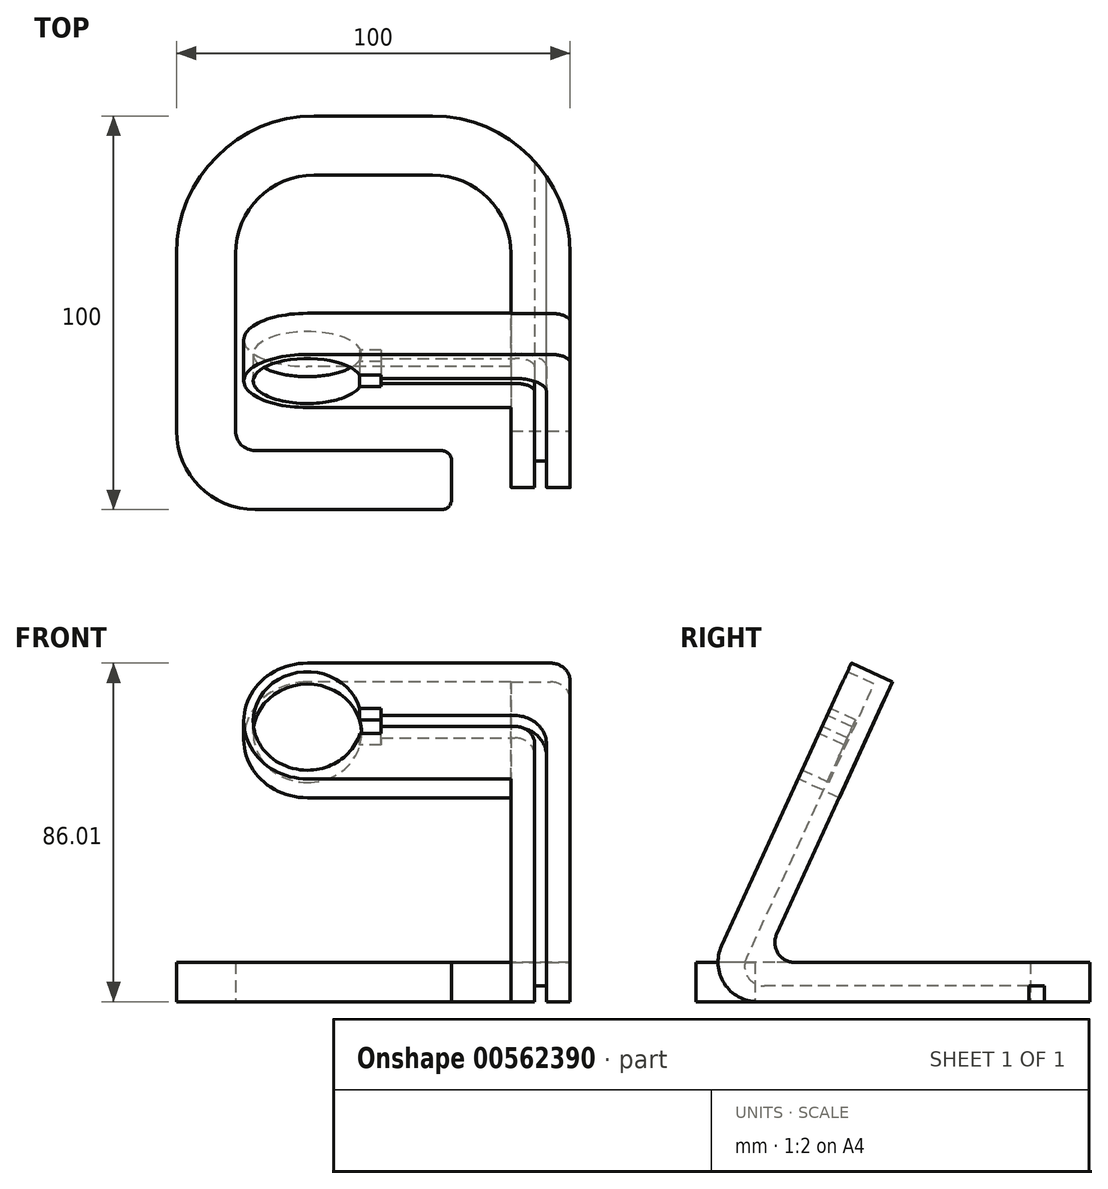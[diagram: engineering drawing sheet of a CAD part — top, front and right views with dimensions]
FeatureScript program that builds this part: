
annotation { "Feature Type Name" : "Feature", "Feature Type Description" : "" }
export const myFeature = defineFeature(function(context is Context, id is Id, definition is map)
    precondition{}
    {
        {
            var Q0;
            Q0=qCreatedBy(makeId("Top.planeOp"),FACE);
            var sketch = newSketch(context, id + "F0", { "sketchPlane" : qUnion([Q0])});
            skLineSegment(sketch, "E0.bottom", {"start": v(15, 50) * mm, "end": v(-15, 50) * mm});
            skLineSegment(sketch, "E0.top", {"start": v(50, -50) * mm, "end": v(35, -50) * mm});
            skLineSegment(sketch, "E0.left", {"start": v(50, 15) * mm, "end": v(50, -50) * mm});
            skLineSegment(sketch, "E0.right", {"start": v(-50, 15) * mm, "end": v(-50, -30) * mm});
            skPoint(sketch, "E0.middle", {"position": v(0, 0) * mm});
            skPoint(sketch, "E1.visualSharp", {"position": v(-50, -50) * mm});
            skArc(sketch, "E1.filletArc", {"start": v(-50, -30) * mm, "mid": v(-44.14, -44.14) * mm, "end": v(-30, -50) * mm});
            skPoint(sketch, "E2.visualSharp", {"position": v(-50, 50) * mm});
            skArc(sketch, "E2.filletArc", {"start": v(-15, 50) * mm, "mid": v(-39.75, 39.75) * mm, "end": v(-50, 15) * mm});
            skPoint(sketch, "E3.visualSharp", {"position": v(50, -50) * mm});
            skPoint(sketch, "E4.visualSharp", {"position": v(50, 50) * mm});
            skArc(sketch, "E4.filletArc", {"start": v(50, 15) * mm, "mid": v(39.75, 39.75) * mm, "end": v(15, 50) * mm});
            skLineSegment(sketch, "E5.0", {"start": v(-35, 15) * mm, "end": v(-35, -30) * mm});
            skLineSegment(sketch, "E6.0", {"start": v(17.36, -35) * mm, "end": v(-30, -35) * mm});
            skLineSegment(sketch, "E7.0", {"start": v(35, 15) * mm, "end": v(35, -35) * mm});
            skLineSegment(sketch, "E8.0", {"start": v(15, 35) * mm, "end": v(-15, 35) * mm});
            skPoint(sketch, "E9.visualSharp", {"position": v(-35, -35) * mm});
            skArc(sketch, "E9.filletArc", {"start": v(-35, -30) * mm, "mid": v(-33.54, -33.54) * mm, "end": v(-30, -35) * mm});
            skPoint(sketch, "E10.visualSharp", {"position": v(-35, 35) * mm});
            skArc(sketch, "E10.filletArc", {"start": v(-15, 35) * mm, "mid": v(-29.14, 29.14) * mm, "end": v(-35, 15) * mm});
            skPoint(sketch, "E11.visualSharp", {"position": v(35, 35) * mm});
            skArc(sketch, "E11.filletArc", {"start": v(35, 15) * mm, "mid": v(29.14, 29.14) * mm, "end": v(15, 35) * mm});
            skLineSegment(sketch, "E12", {"start": v(19.86, -37.5) * mm, "end": v(19.86, -47.5) * mm});
            skLineSegment(sketch, "E13", {"start": v(35, -50) * mm, "end": v(35, -35) * mm});
            skLineSegment(sketch, "E14.trimOffspring", {"start": v(17.36, -50) * mm, "end": v(-30, -50) * mm});
            skPoint(sketch, "E15.visualSharp", {"position": v(19.86, -35) * mm});
            skArc(sketch, "E15.filletArc", {"start": v(19.86, -37.5) * mm, "mid": v(19.13, -35.73) * mm, "end": v(17.36, -35) * mm});
            skPoint(sketch, "E16.visualSharp", {"position": v(19.86, -50) * mm});
            skArc(sketch, "E16.filletArc", {"start": v(17.36, -50) * mm, "mid": v(19.13, -49.27) * mm, "end": v(19.86, -47.5) * mm});
            skSolve(sketch);
        }
        {
            var Q0;
            Q0=makeQuery(id+"F0.imprint","IMPRINT",FACE,{"disambiguationData":[TD([[makeQuery(id+"F0.imprint","IMPRINT",EDGE,{"derivedFrom":sQuery(id+"F0.wireOp",EDGE,"E0.bottom")}),1.0]])]});
            extrude(context, id + "F1", {"entities" : qUnion([Q0]), "depth" : 10 * mm, "offsetDistance" : 25 * mm});
        }
        {
            var Q0;
            Q0=makeQuery(id+"F1.opExtrude","SWEPT_FACE",FACE,{"disambiguationData":[OSD([sQuery(id+"F0.wireOp",EDGE,"E0.left")])]});
            var sketch = newSketch(context, id + "F2", { "sketchPlane" : qUnion([Q0])});
            skLineSegment(sketch, "E17", {"start": v(-43.5, 14.17) * mm, "end": v(-10.57, 86.01) * mm});
            skLineSegment(sketch, "E18", {"start": v(-10.57, 86.01) * mm, "end": v(-0.13, 81.23) * mm});
            skLineSegment(sketch, "E19", {"start": v(-0.13, 81.23) * mm, "end": v(-29.53, 17.08) * mm});
            skLineSegment(sketch, "E20", {"start": v(-18.45, 10) * mm, "end": v(-24.99, 10) * mm});
            skLineSegment(sketch, "E21", {"start": v(-18.45, 0) * mm, "end": v(-34.41, 0) * mm});
            skLineSegment(sketch, "E22", {"start": v(-18.45, 0) * mm, "end": v(-18.45, 10) * mm});
            skArc(sketch, "E23.filletArc", {"start": v(-29.53, 17.08) * mm, "mid": v(-29.2, 12.3) * mm, "end": v(-24.99, 10) * mm});
            skPoint(sketch, "E24.visualSharp", {"position": v(-50, 0) * mm});
            skArc(sketch, "E24.filletArc", {"start": v(-43.5, 14.17) * mm, "mid": v(-42.83, 4.6) * mm, "end": v(-34.41, 0) * mm});
            skSolve(sketch);
        }
        {
            var Q0;
            {var subQ1=sQuery(id+"F0.wireOp",EDGE,"E0.left");var subQ6=makeQuery(id+"F1.opExtrude","SWEPT_EDGE",EDGE,{"disambiguationData":[OSD([sQuery(id+"F0.wireOp",EDGE,"E0.top"),subQ1])]});Q0=makeQuery(id+"F2.imprint","IMPRINT",FACE,{"disambiguationData":[TD([[makeQuery(id+"F2.imprint","IMPRINT",EDGE,{"derivedFrom":subQ6}),1.0]])]});}
            extrude(context, id + "F3", {"entities" : qUnion([Q0]), "operationType" : NewBodyOperationType.REMOVE, "oppositeDirection" : true, "depth" : 25 * mm, "offsetDistance" : 25 * mm});
        }
        {
            var Q0;
            {var subQ1=sQuery(id+"F2.wireOp",EDGE,"E17");Q0=makeQuery(id+"F2.imprint","IMPRINT",FACE,{"disambiguationData":[TD([[makeQuery(id+"F2.imprint","IMPRINT",EDGE,{"derivedFrom":subQ1}),-1.0]])]});}
            extrude(context, id + "F4", {"entities" : qUnion([Q0]), "operationType" : NewBodyOperationType.ADD, "oppositeDirection" : true, "depth" : 15 * mm, "offsetDistance" : 25 * mm});
        }
        {
            var Q0;
            Q0=makeQuery(id+"F4.opExtrude","SWEPT_FACE",FACE,{"disambiguationData":[OSD([sQuery(id+"F2.wireOp",EDGE,"E17")])]});
            var sketch = newSketch(context, id + "F5", { "sketchPlane" : qUnion([Q0])});
            skLineSegment(sketch, "E25.bottom", {"start": v(50, 73.79) * mm, "end": v(-16.75, 73.79) * mm});
            skLineSegment(sketch, "E25.top", {"start": v(50, 41.44) * mm, "end": v(-16.75, 41.44) * mm});
            skLineSegment(sketch, "E25.left", {"start": v(50, 73.79) * mm, "end": v(50, 41.44) * mm});
            skCircle(sketch, "E26", {"center": v(-16.75, 57.61) * mm, "radius": 16.17 * mm});
            skPoint(sketch, "E27.visualSharp", {"position": v(50, 73.79) * mm});
            skCircle(sketch, "E28", {"center": v(-16.75, 57.61) * mm, "radius": 13.75 * mm});
            skSolve(sketch);
        }
        {
            var Q0;
            Q0=makeQuery(id+"F5.imprint","IMPRINT",FACE,{"disambiguationData":[TD([[makeQuery(id+"F5.imprint","IMPRINT",EDGE,{"derivedFrom":sQuery(id+"F5.wireOp",EDGE,"E28")}),-1.0]])]});
            var Q1;
            Q1=makeQuery(id+"F5.imprint","IMPRINT",FACE,{"disambiguationData":[TD([[makeQuery(id+"F5.imprint","IMPRINT",EDGE,{"derivedFrom":sQuery(id+"F5.wireOp",EDGE,"E28")}),1.0]])]});
            var Q2;
            Q2=makeQuery(id+"F5.imprint","IMPRINT",FACE,{"disambiguationData":[TD([[makeQuery(id+"F5.imprint","IMPRINT",EDGE,{"derivedFrom":sQuery(id+"F5.wireOp",EDGE,"ab50c3b4-7159-4a78-a1d6-39594553cd38")}),1.0]])]});
            var Q3;
            {var subQ0=sQuery(id+"F5.wireOp",EDGE,"E25.bottom");var subQ3=sQuery(id+"F5.wireOp",EDGE,"E26");var subQ4=makeQuery(id+"F5.imprint","INTERSECT",VERTEX,{"derivedFrom":[subQ0,subQ3]});Q3=makeQuery(id+"F5.imprint","IMPRINT",FACE,{"disambiguationData":[TD([[makeQuery(id+"F5.imprint","IMPRINT",EDGE,{"disambiguationData":[TD([[subQ4,1.0]])],"derivedFrom":subQ0}),1.0]])]});}
            extrude(context, id + "F6", {"entities" : qUnion([Q0, Q1, Q2, Q3]), "operationType" : NewBodyOperationType.ADD, "oppositeDirection" : true, "depth" : 11.5 * mm, "offsetDistance" : 25 * mm});
        }
        {
            var Q0;
            Q0=makeQuery(id+"F5.imprint","IMPRINT",FACE,{"disambiguationData":[TD([[makeQuery(id+"F5.imprint","IMPRINT",EDGE,{"derivedFrom":sQuery(id+"F5.wireOp",EDGE,"ab50c3b4-7159-4a78-a1d6-39594553cd38")}),1.0]])]});
            var Q1;
            Q1=makeQuery(id+"F5.imprint","IMPRINT",FACE,{"disambiguationData":[TD([[makeQuery(id+"F5.imprint","IMPRINT",EDGE,{"derivedFrom":sQuery(id+"F5.wireOp",EDGE,"E28")}),1.0]])]});
            extrude(context, id + "F7", {"entities" : qUnion([Q0, Q1]), "operationType" : NewBodyOperationType.REMOVE, "oppositeDirection" : true, "depth" : 7.5 * mm, "offsetDistance" : 25 * mm});
        }
        {
            var Q0;
            {var subQ0=sQuery(id+"F2.wireOp",EDGE,"E17");Q0=makeQuery(id+"F6.boolean.opBoolean","MERGE",FACE,{"derivedFrom":[makeQuery(id+"F4.opExtrude","SWEPT_FACE",FACE,{"disambiguationData":[OSD([subQ0])]}),makeQuery(id+"F6.opExtrude","CAP_FACE",FACE,{"disambiguationData":[OSD([subQ0,sQuery(id+"F5.wireOp",EDGE,"E25.bottom"),sQuery(id+"F5.wireOp",EDGE,"E25.top"),sQuery(id+"F5.wireOp",EDGE,"E26")])],"isStart":true})]});}
            var sketch = newSketch(context, id + "F8", { "sketchPlane" : qUnion([Q0])});
            skLineSegment(sketch, "E29", {"start": v(-3, 57.61) * mm, "end": v(42.5, 57.61) * mm, "construction": true});
            skPoint(sketch, "E29.startSnap0", {"position": v(-32.92, 57.61) * mm});
            skLineSegment(sketch, "E30", {"start": v(42.5, 57.61) * mm, "end": v(42.5, -17.42) * mm, "construction": true});
            skPoint(sketch, "E30.startSnap0", {"position": v(42.5, -5.25) * mm});
            skPoint(sketch, "E30.endSnap0", {"position": v(42.5, -5.25) * mm});
            skLineSegment(sketch, "E31", {"start": v(2, 59.11) * mm, "end": v(36, 59.11) * mm});
            skLineSegment(sketch, "E32", {"start": v(2, 56.11) * mm, "end": v(36, 56.11) * mm});
            skLineSegment(sketch, "E33", {"start": v(2, 59.11) * mm, "end": v(2, 56.11) * mm});
            skLineSegment(sketch, "E34.bottom", {"start": v(2, 61.11) * mm, "end": v(-6.68, 61.11) * mm});
            skLineSegment(sketch, "E34.top", {"start": v(2, 54.11) * mm, "end": v(-6.68, 54.11) * mm});
            skLineSegment(sketch, "E34.left", {"start": v(2, 61.11) * mm, "end": v(2, 54.11) * mm});
            skLineSegment(sketch, "E34.right", {"start": v(-6.68, 61.11) * mm, "end": v(-6.68, 54.11) * mm});
            skLineSegment(sketch, "E35", {"start": v(41, 51.11) * mm, "end": v(41, -17.42) * mm});
            skLineSegment(sketch, "E36", {"start": v(41, -17.42) * mm, "end": v(44, -17.42) * mm});
            skLineSegment(sketch, "E37", {"start": v(44, -17.42) * mm, "end": v(44, 51.11) * mm});
            skPoint(sketch, "E38.visualSharp", {"position": v(41, 56.11) * mm});
            skArc(sketch, "E38.filletArc", {"start": v(41, 51.11) * mm, "mid": v(39.54, 54.65) * mm, "end": v(36, 56.11) * mm});
            skPoint(sketch, "E39.visualSharp", {"position": v(44, 59.11) * mm});
            skArc(sketch, "E39.filletArc", {"start": v(44, 51.11) * mm, "mid": v(41.66, 56.77) * mm, "end": v(36, 59.11) * mm});
            skSolve(sketch);
        }
        {
            var Q0;
            {var subQ0=sQuery(id+"F8.wireOp",EDGE,"E34.left");var subQ2=sQuery(id+"F8.wireOp",EDGE,"E34.bottom");var subQ3=makeQuery(id+"F8.imprint","INTERSECT",VERTEX,{"derivedFrom":[subQ2,subQ0]});Q0=makeQuery(id+"F8.imprint","IMPRINT",FACE,{"disambiguationData":[TD([[makeQuery(id+"F8.imprint","IMPRINT",EDGE,{"disambiguationData":[TD([[subQ3,-1.0]])],"derivedFrom":subQ2}),1.0]])]});}
            var Q1;
            {var subQ1=sQuery(id+"F8.wireOp",EDGE,"E31");Q1=makeQuery(id+"F8.imprint","IMPRINT",FACE,{"disambiguationData":[TD([[makeQuery(id+"F8.imprint","IMPRINT",EDGE,{"derivedFrom":subQ1}),-1.0]])]});}
            var Q2;
            {var subQ0=sQuery(id+"F8.wireOp",EDGE,"E36");Q2=makeQuery(id+"F8.imprint","IMPRINT",FACE,{"disambiguationData":[TD([[makeQuery(id+"F8.imprint","IMPRINT",EDGE,{"derivedFrom":subQ0}),1.0]])]});}
            extrude(context, id + "F9", {"entities" : qUnion([Q0, Q1, Q2]), "operationType" : NewBodyOperationType.REMOVE, "oppositeDirection" : true, "depth" : 7 * mm, "offsetDistance" : 25 * mm});
        }
        {
            var Q0;
            Q0=makeQuery(id+"F1.opExtrude","CAP_FACE",FACE,{"disambiguationData":[OSD([sQuery(id+"F0.wireOp",EDGE,"E0.bottom"),sQuery(id+"F0.wireOp",EDGE,"E0.top"),sQuery(id+"F0.wireOp",EDGE,"E0.left"),sQuery(id+"F0.wireOp",EDGE,"E0.right"),sQuery(id+"F0.wireOp",EDGE,"E1.filletArc"),sQuery(id+"F0.wireOp",EDGE,"E2.filletArc"),sQuery(id+"F0.wireOp",EDGE,"E4.filletArc"),sQuery(id+"F0.wireOp",EDGE,"E5.0"),sQuery(id+"F0.wireOp",EDGE,"E6.0"),sQuery(id+"F0.wireOp",EDGE,"E7.0"),sQuery(id+"F0.wireOp",EDGE,"E8.0"),sQuery(id+"F0.wireOp",EDGE,"E9.filletArc"),sQuery(id+"F0.wireOp",EDGE,"E10.filletArc"),sQuery(id+"F0.wireOp",EDGE,"E11.filletArc"),sQuery(id+"F0.wireOp",EDGE,"E12"),sQuery(id+"F0.wireOp",EDGE,"E13"),sQuery(id+"F0.wireOp",EDGE,"E14.trimOffspring"),sQuery(id+"F0.wireOp",EDGE,"E15.filletArc"),sQuery(id+"F0.wireOp",EDGE,"E16.filletArc")])],"isStart":true});
            var sketch = newSketch(context, id + "F10", { "sketchPlane" : qUnion([Q0])});
            skLineSegment(sketch, "E40", {"start": v(42.5, 34.41) * mm, "end": v(42.5, -49.23) * mm, "construction": true});
            skLineSegment(sketch, "E41", {"start": v(41, 34.41) * mm, "end": v(41, -49.23) * mm});
            skLineSegment(sketch, "E42", {"start": v(44, -49.23) * mm, "end": v(44, 34.41) * mm});
            skLineSegment(sketch, "E43", {"start": v(41, 34.41) * mm, "end": v(41, 42.4) * mm});
            skLineSegment(sketch, "E44", {"start": v(41, 42.4) * mm, "end": v(44, 42.4) * mm});
            skLineSegment(sketch, "E45", {"start": v(44, 42.4) * mm, "end": v(44, 34.41) * mm});
            skLineSegment(sketch, "E46", {"start": v(41, 34.41) * mm, "end": v(44, 34.41) * mm});
            skSolve(sketch);
        }
        {
            var Q0;
            Q0=makeQuery(id+"F10.imprint","IMPRINT",FACE,{"disambiguationData":[TD([[makeQuery(id+"F10.imprint","IMPRINT",EDGE,{"derivedFrom":sQuery(id+"F10.wireOp",EDGE,"E43")}),-1.0]])]});
            var Q1;
            {var subQ0=sQuery(id+"F10.wireOp",EDGE,"E46");Q1=makeQuery(id+"F10.imprint","IMPRINT",FACE,{"disambiguationData":[TD([[makeQuery(id+"F10.imprint","IMPRINT",EDGE,{"derivedFrom":subQ0}),-1.0]])]});}
            extrude(context, id + "F11", {"entities" : qUnion([Q0, Q1]), "operationType" : NewBodyOperationType.REMOVE, "oppositeDirection" : true, "depth" : 4 * mm, "offsetDistance" : 25 * mm});
        }
        {
            var Q0;
            Q0=makeQuery(id+"F11.boolean.opBoolean","INTERSECT",EDGE,{"derivedFrom":[makeQuery(id+"F9.boolean.opBoolean","COPY",FACE,{"derivedFrom":makeQuery(id+"F9.opExtrude","CAP_FACE",FACE,{"disambiguationData":[OSD([sQuery(id+"F5.wireOp",EDGE,"E28"),sQuery(id+"F8.wireOp",EDGE,"E31"),sQuery(id+"F8.wireOp",EDGE,"E32"),sQuery(id+"F8.wireOp",EDGE,"E34.bottom"),sQuery(id+"F8.wireOp",EDGE,"E34.top"),sQuery(id+"F8.wireOp",EDGE,"E34.left"),sQuery(id+"F8.wireOp",EDGE,"E35"),sQuery(id+"F8.wireOp",EDGE,"E36"),sQuery(id+"F8.wireOp",EDGE,"E37"),sQuery(id+"F8.wireOp",EDGE,"E38.filletArc"),sQuery(id+"F8.wireOp",EDGE,"E39.filletArc")])],"isStart":false})}),makeQuery(id+"F11.opExtrude","CAP_FACE",FACE,{"disambiguationData":[OSD([sQuery(id+"F0.wireOp",EDGE,"E4.filletArc"),sQuery(id+"F10.wireOp",EDGE,"E41"),sQuery(id+"F10.wireOp",EDGE,"E42"),sQuery(id+"F10.wireOp",EDGE,"E43"),sQuery(id+"F10.wireOp",EDGE,"E44"),sQuery(id+"F10.wireOp",EDGE,"E45")])],"isStart":false})]});
            fillet(context, id + "F12", {"entities" : qUnion([Q0]), "radius" : 5 * mm, "tangentPropagation" : true, "allowEdgeOverflow" : false});
        }
        {
            var Q0;
            Q0=makeQuery(id+"F4.opExtrude","CAP_EDGE",EDGE,{"disambiguationData":[OSD([sQuery(id+"F2.wireOp",EDGE,"E18")])],"isStart":true});
            fillet(context, id + "F13", {"entities" : qUnion([Q0]), "radius" : 5 * mm, "tangentPropagation" : true, "allowEdgeOverflow" : false});
        }
    });
